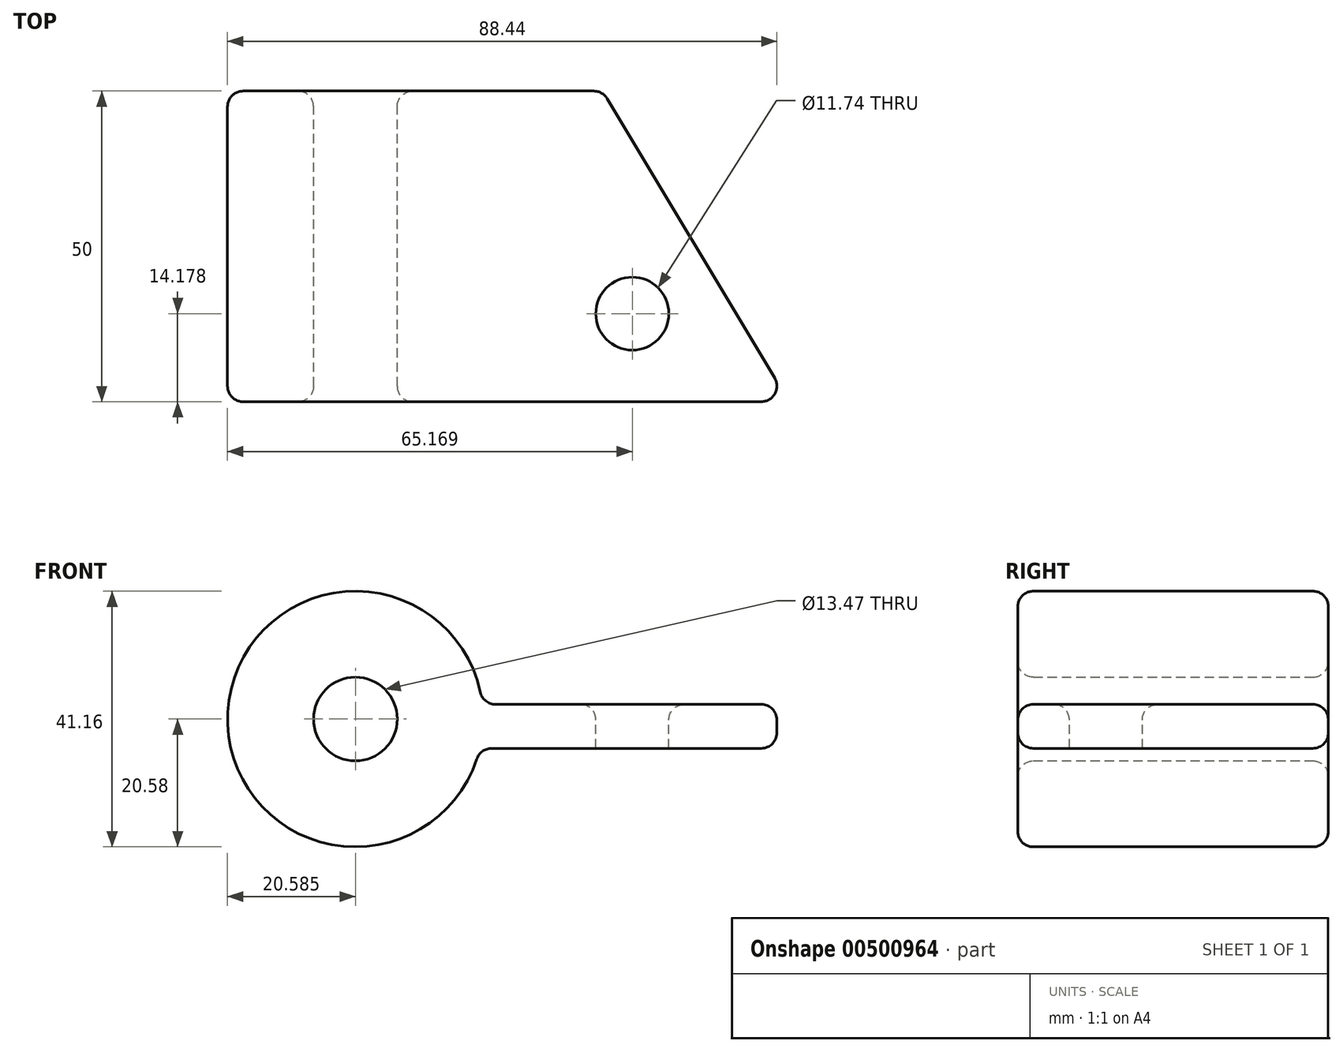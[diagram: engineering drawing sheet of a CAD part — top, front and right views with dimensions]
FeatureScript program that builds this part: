
annotation { "Feature Type Name" : "Feature", "Feature Type Description" : "" }
export const myFeature = defineFeature(function(context is Context, id is Id, definition is map)
    precondition{}
    {
        {
            var Q0;
            Q0=qCreatedBy(makeId("Front.planeOp"),FACE);
            var sketch = newSketch(context, id + "F0", { "sketchPlane" : qUnion([Q0])});
            skCircle(sketch, "E0", {"center": v(-44.76, 6.82) * mm, "radius": 20.58 * mm});
            skCircle(sketch, "E1", {"center": v(-44.76, 6.82) * mm, "radius": 6.74 * mm});
            skSolve(sketch);
        }
        {
            var Q0;
            Q0=makeQuery(id+"F0.imprint","IMPRINT",FACE,{"disambiguationData":[TD([[makeQuery(id+"F0.imprint","IMPRINT",EDGE,{"derivedFrom":sQuery(id+"F0.wireOp",EDGE,"E0")}),1.0]])]});
            extrude(context, id + "F1", {"entities" : qUnion([Q0]), "depth" : 50 * mm});
        }
        {
            var Q0;
            Q0=qCreatedBy(makeId("Right.planeOp"),FACE);
            var sketch = newSketch(context, id + "F2", { "sketchPlane" : qUnion([Q0])});
            skLineSegment(sketch, "E2.bottom", {"start": v(-50.14, 9.18) * mm, "end": v(0, 9.18) * mm});
            skLineSegment(sketch, "E2.top", {"start": v(-50.14, 2.1) * mm, "end": v(0, 2.1) * mm});
            skLineSegment(sketch, "E2.left", {"start": v(-50.14, 9.18) * mm, "end": v(-50.14, 2.1) * mm});
            skLineSegment(sketch, "E2.right", {"start": v(0, 9.18) * mm, "end": v(0, 2.1) * mm});
            skSolve(sketch);
        }
        {
            var Q0;
            Q0=makeQuery(id+"F2.imprint","IMPRINT",FACE,{"disambiguationData":[TD([[makeQuery(id+"F2.imprint","IMPRINT",EDGE,{"derivedFrom":sQuery(id+"F2.wireOp",EDGE,"E2.bottom")}),-1.0]])]});
            extrude(context, id + "F3", {"entities" : qUnion([Q0]), "oppositeDirection" : true, "depth" : 25 * mm});
        }
        {
            var Q0;
            Q0=makeQuery(id+"F3.opExtrude","SWEPT_BODY",BODY,{"disambiguationData":[OSD([sQuery(id+"F2.wireOp",EDGE,"E2.bottom"),sQuery(id+"F2.wireOp",EDGE,"E2.top"),sQuery(id+"F2.wireOp",EDGE,"E2.left"),sQuery(id+"F2.wireOp",EDGE,"E2.right")])]});
            var Q1;
            Q1=makeQuery(id+"F1.opExtrude","SWEPT_BODY",BODY,{"disambiguationData":[OSD([sQuery(id+"F0.wireOp",EDGE,"E0"),sQuery(id+"F0.wireOp",EDGE,"E1")])]});
            booleanBodies(context, id + "F4", {"operationType" : BooleanOperationType.UNION, "tools" : qUnion([Q0, Q1])});
        }
        {
            var Q0;
            Q0=makeQuery(id+"F3.opExtrude","CAP_FACE",FACE,{"disambiguationData":[OSD([sQuery(id+"F2.wireOp",EDGE,"E2.bottom"),sQuery(id+"F2.wireOp",EDGE,"E2.top"),sQuery(id+"F2.wireOp",EDGE,"E2.left"),sQuery(id+"F2.wireOp",EDGE,"E2.right")])],"isStart":true});
            extrude(context, id + "F5", {"entities" : qUnion([Q0]), "operationType" : NewBodyOperationType.ADD, "depth" : 25 * mm});
        }
        {
            var Q0;
            {var subQ0=sQuery(id+"F2.wireOp",EDGE,"E2.left");Q0=makeQuery(id+"F5.boolean.opBoolean","MERGE",FACE,{"derivedFrom":[makeQuery(id+"F3.opExtrude","SWEPT_FACE",FACE,{"disambiguationData":[OSD([subQ0])]}),makeQuery(id+"F5.opExtrude","SWEPT_FACE",FACE,{"disambiguationData":[OSD([subQ0])]})]});}
            var Q1;
            Q1=makeQuery(id+"F1.opExtrude","CAP_FACE",FACE,{"disambiguationData":[OSD([sQuery(id+"F0.wireOp",EDGE,"E0"),sQuery(id+"F0.wireOp",EDGE,"E1")])],"isStart":false});
            extrude(context, id + "F6", {"entities" : qUnion([Q0]), "operationType" : NewBodyOperationType.REMOVE, "endBound" : BoundingType.UP_TO_SURFACE, "oppositeDirection" : true, "endBoundEntityFace" : qUnion([Q1]), "depth" : 25 * mm});
        }
        {
            var Q0;
            {var subQ0=sQuery(id+"F2.wireOp",EDGE,"E2.bottom");Q0=makeQuery(id+"F5.boolean.opBoolean","MERGE",FACE,{"derivedFrom":[makeQuery(id+"F3.opExtrude","SWEPT_FACE",FACE,{"disambiguationData":[OSD([subQ0])]}),makeQuery(id+"F5.opExtrude","SWEPT_FACE",FACE,{"disambiguationData":[OSD([subQ0])]})]});}
            var sketch = newSketch(context, id + "F7", { "sketchPlane" : qUnion([Q0])});
            skLineSegment(sketch, "E3", {"start": v(25, -50) * mm, "end": v(-4.96, 0) * mm});
            skSolve(sketch);
        }
        {
            var Q0;
            {var subQ3=sQuery(id+"F7.wireOp",EDGE,"E3");Q0=makeQuery(id+"F7.imprint","IMPRINT",FACE,{"disambiguationData":[TD([[makeQuery(id+"F7.imprint","IMPRINT",EDGE,{"derivedFrom":subQ3}),-1.0]])]});}
            extrude(context, id + "F8", {"entities" : qUnion([Q0]), "operationType" : NewBodyOperationType.REMOVE, "endBound" : BoundingType.THROUGH_ALL, "oppositeDirection" : true, "depth" : 25 * mm});
        }
        {
            var Q0;
            {var subQ0=sQuery(id+"F2.wireOp",EDGE,"E2.bottom");Q0=makeQuery(id+"F5.boolean.opBoolean","MERGE",FACE,{"derivedFrom":[makeQuery(id+"F3.opExtrude","SWEPT_FACE",FACE,{"disambiguationData":[OSD([subQ0])]}),makeQuery(id+"F5.opExtrude","SWEPT_FACE",FACE,{"disambiguationData":[OSD([subQ0])]})]});}
            var sketch = newSketch(context, id + "F9", { "sketchPlane" : qUnion([Q0])});
            skCircle(sketch, "E4", {"center": v(-0.18, -35.82) * mm, "radius": 5.87 * mm});
            skSolve(sketch);
        }
        {
            var Q0;
            Q0=makeQuery(id+"F9.imprint","IMPRINT",FACE,{"disambiguationData":[TD([[makeQuery(id+"F9.imprint","IMPRINT",EDGE,{"derivedFrom":sQuery(id+"F9.wireOp",EDGE,"E4")}),1.0]])]});
            extrude(context, id + "F10", {"entities" : qUnion([Q0]), "operationType" : NewBodyOperationType.REMOVE, "endBound" : BoundingType.THROUGH_ALL, "oppositeDirection" : true, "depth" : 25 * mm});
        }
        {
            var Q0;
            {var subQ0=sQuery(id+"F0.wireOp",EDGE,"E1");var subQ1=sQuery(id+"F0.wireOp",EDGE,"E0");Q0=makeQuery(id+"F6.boolean.opBoolean","MERGE",FACE,{"derivedFrom":[makeQuery(id+"F1.opExtrude","CAP_FACE",FACE,{"disambiguationData":[OSD([subQ1,subQ0])],"isStart":false}),makeQuery(id+"F6.opExtrude","CAP_FACE",FACE,{"disambiguationData":[OSD([subQ1,subQ0])],"isStart":false})]});}
            var Q1;
            Q1=makeQuery(id+"F1.opExtrude","SWEPT_FACE",FACE,{"disambiguationData":[OSD([sQuery(id+"F0.wireOp",EDGE,"E1")])]});
            var Q2;
            {var subQ0=sQuery(id+"F2.wireOp",EDGE,"E2.bottom");Q2=makeQuery(id+"F5.boolean.opBoolean","MERGE",FACE,{"derivedFrom":[makeQuery(id+"F3.opExtrude","SWEPT_FACE",FACE,{"disambiguationData":[OSD([subQ0])]}),makeQuery(id+"F5.opExtrude","SWEPT_FACE",FACE,{"disambiguationData":[OSD([subQ0])]})]});}
            var Q3;
            Q3=makeQuery(id+"F8.boolean.opBoolean","COPY",FACE,{"derivedFrom":makeQuery(id+"F8.opExtrude","SWEPT_FACE",FACE,{"disambiguationData":[OSD([sQuery(id+"F7.wireOp",EDGE,"E3")])]})});
            var Q4;
            Q4=makeQuery(id+"F1.opExtrude","SWEPT_FACE",FACE,{"disambiguationData":[OSD([sQuery(id+"F0.wireOp",EDGE,"E0")])]});
            var Q5;
            {var subQ0=sQuery(id+"F2.wireOp",EDGE,"E2.right");Q5=makeQuery(id+"F5.boolean.opBoolean","MERGE",FACE,{"derivedFrom":[makeQuery(id+"F4.opBoolean","MERGE",FACE,{"derivedFrom":[makeQuery(id+"F1.opExtrude","CAP_FACE",FACE,{"disambiguationData":[OSD([sQuery(id+"F0.wireOp",EDGE,"E0"),sQuery(id+"F0.wireOp",EDGE,"E1")])],"isStart":true}),makeQuery(id+"F3.opExtrude","SWEPT_FACE",FACE,{"disambiguationData":[OSD([subQ0])]})]}),makeQuery(id+"F5.opExtrude","SWEPT_FACE",FACE,{"disambiguationData":[OSD([subQ0])]})]});}
            fillet(context, id + "F11", {"entities" : qUnion([Q0, Q1, Q2, Q3, Q4, Q5]), "radius" : 2.5 * mm, "tangentPropagation" : true, "allowEdgeOverflow" : false});
        }
    });
